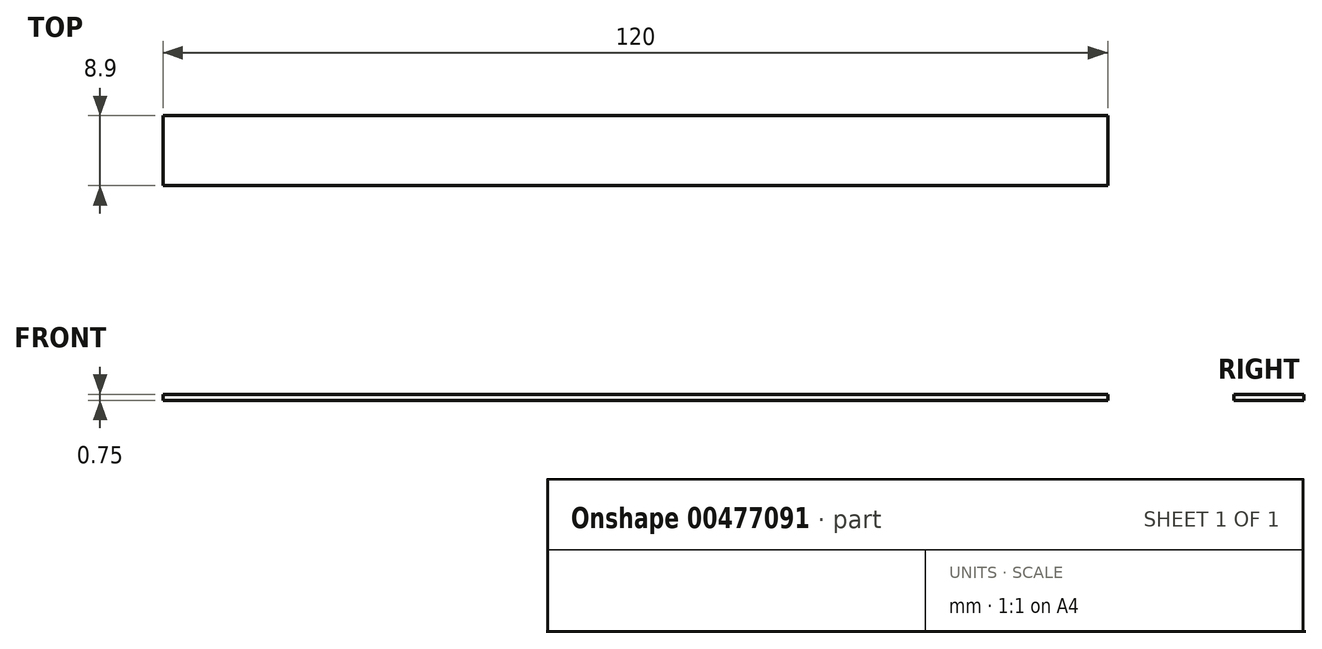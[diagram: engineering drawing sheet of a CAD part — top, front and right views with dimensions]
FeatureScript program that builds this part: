
annotation { "Feature Type Name" : "Feature", "Feature Type Description" : "" }
export const myFeature = defineFeature(function(context is Context, id is Id, definition is map)
    precondition{}
    {
        {
            var Q0;
            Q0=qCreatedBy(makeId("Top.planeOp"),FACE);
            var sketch = newSketch(context, id + "F0", { "sketchPlane" : qUnion([Q0])});
            skLineSegment(sketch, "E0.bottom", {"start": v(-49.98, -5.86) * mm, "end": v(70.02, -5.86) * mm});
            skLineSegment(sketch, "E0.top", {"start": v(-49.98, -14.76) * mm, "end": v(70.02, -14.76) * mm});
            skLineSegment(sketch, "E0.left", {"start": v(-49.98, -5.86) * mm, "end": v(-49.98, -14.76) * mm});
            skLineSegment(sketch, "E0.right", {"start": v(70.02, -5.86) * mm, "end": v(70.02, -14.76) * mm});
            skSolve(sketch);
        }
        {
            var Q0;
            Q0 = qSketchRegion(id + "F0", true);
            extrude(context, id + "F1", {"entities" : qUnion([Q0]), "depth" : 0.75 * mm});
        }
    });
